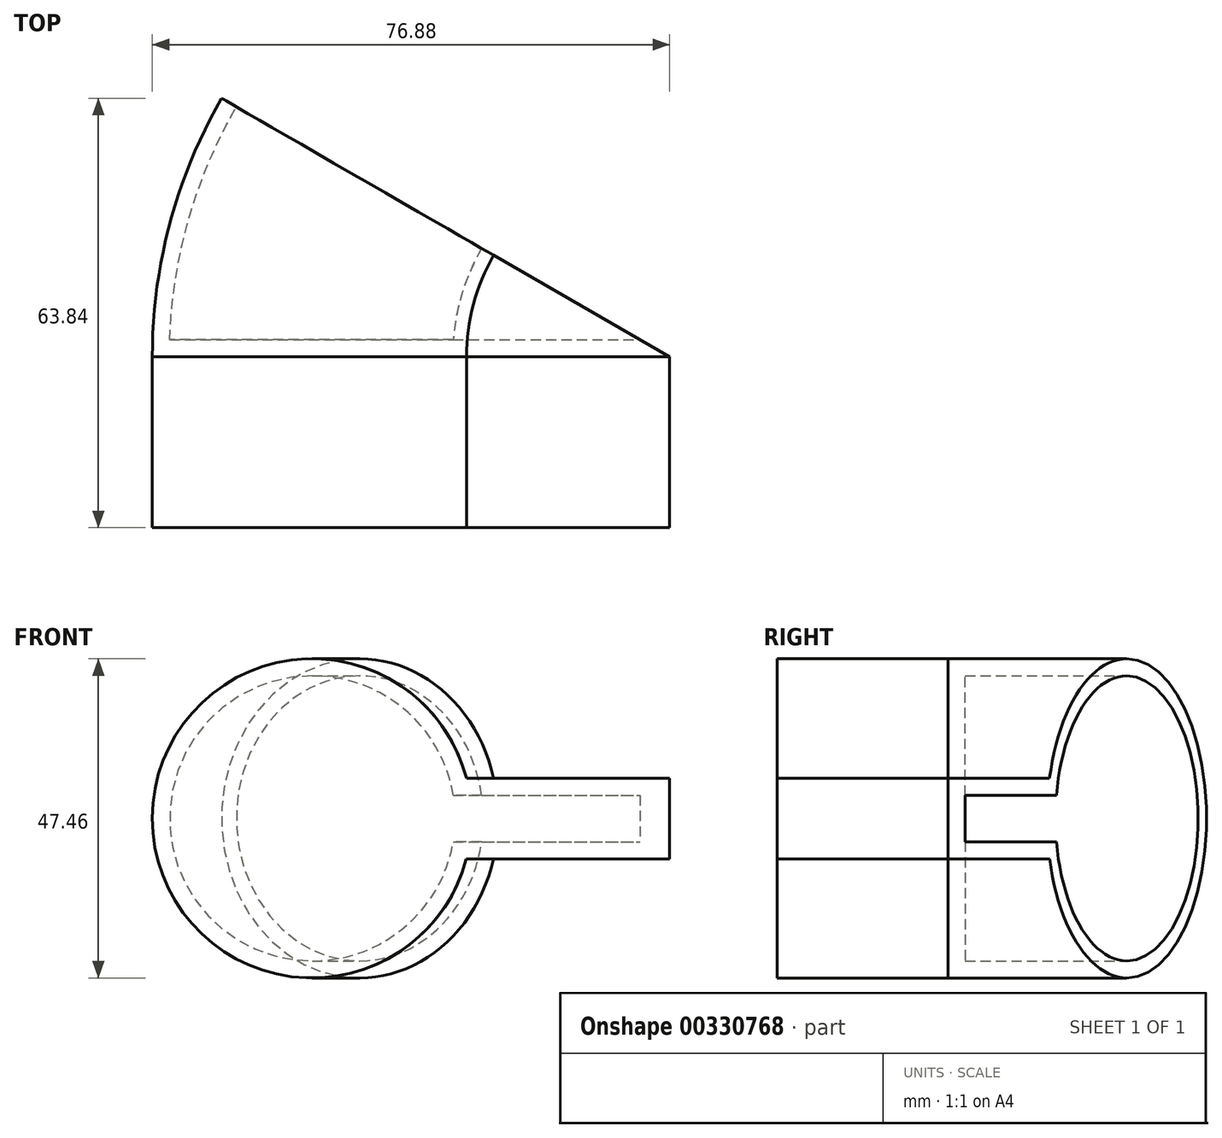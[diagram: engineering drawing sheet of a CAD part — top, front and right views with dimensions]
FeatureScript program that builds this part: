
annotation { "Feature Type Name" : "Feature", "Feature Type Description" : "" }
export const myFeature = defineFeature(function(context is Context, id is Id, definition is map)
    precondition{}
    {
        {
            var Q0;
            Q0=qCreatedBy(makeId("Front.planeOp"),FACE);
            var sketch = newSketch(context, id + "F0", { "sketchPlane" : qUnion([Q0])});
            skArc(sketch, "E0", {"start": v(22.97, 5.96) * mm, "mid": v(-23.73, 0.04) * mm, "end": v(22.95, -6.02) * mm});
            skLineSegment(sketch, "E1.bottom", {"start": v(22.97, 5.96) * mm, "end": v(53.15, 5.96) * mm});
            skLineSegment(sketch, "E1.top", {"start": v(22.95, -6.02) * mm, "end": v(53.15, -6.02) * mm});
            skLineSegment(sketch, "E1.right", {"start": v(53.15, 5.96) * mm, "end": v(53.15, -6.02) * mm});
            skSolve(sketch);
        }
        {
            var Q0;
            Q0 = qSketchRegion(id + "F0", true);
            extrude(context, id + "F1", {"entities" : qUnion([Q0]), "depth" : 25.4 * mm});
        }
        {
            var Q0;
            Q0 = qSketchRegion(id + "F0", true);
            var Q1;
            Q1=sQuery(id+"F0.wireOp",EDGE,"E1.right");
            revolve(context, id + "F2", {"entities" : qUnion([Q0]), "axis" : qUnion([Q1]), "revolveType" : RevolveType.ONE_DIRECTION, "angle" : 30 * degree});
        }
        {
            var Q0;
            Q0=makeQuery(id+"F2.opRevolve","CAP_FACE",FACE,{"disambiguationData":[OSD([sQuery(id+"F0.wireOp",EDGE,"E0"),sQuery(id+"F0.wireOp",EDGE,"E1.bottom"),sQuery(id+"F0.wireOp",EDGE,"E1.top"),sQuery(id+"F0.wireOp",EDGE,"E1.right")])],"isStart":false});
            shell(context, id + "F3", {"entities" : qUnion([Q0]), "thickness" : 2.54 * mm});
        }
    });
